# Revit family: Grease_Interceptor-MIFAB-BIG-500 (1)
name_source: partatom
category: Specialty Equipment
units: mm (PartAtom-declared; Revit-internal decimal feet)

## family parameters
Always vertical = No
Cut with Voids When Loaded = No
OmniClass Number = 23.70.50.14.21.14
OmniClass Title = Grease Interceptor
Part Type = Normal
Room Calculation Point = No
Round Connector Dimension = Use Diameter
Shared = Yes
Work Plane-Based = Yes

## types (1)
- BIG-500
    Assembly Code = D2030400
    Default Elevation = 0"
    Description = MIFAB® Series BIG 500 HDPE rotational molded grease interceptor with flow rating of 50 GPM and liquid holding capacity of 55
gallons.
    Finish (Body) = Plastic-MIFAB-Polyethylene
    Finish (Lid) = Metal-MIFAB-Steel
    Finish (Pipe) = Metal-MIFAB-Stainless Steel
    Flow Rate = 50 GPM
    Grease Design Capacity = 250 Lbs. (35 Gallons)
    IAPMO Compliance = Compliance with International Plumbing Code (I.P.C.) / I.C.C.
    Installation Type = On or In Floor
    Length = 37"
    Liquid Holding Capacity = 55 Gallons (7.19 Cu. Ft.)
    Manufacturer = MIFAB
    Model = BIG-500
    Price = Prices may vary. Please consult Manufacturer Representative for most up-to-date price list.
    Product Documentation Link = https://www.mifab.com
    Product Page URL = https://www.mifab.com
    Sediment Capacity = 28 Gallons
    Shipping Weight = 90 lb
    URL = https://www.mifab.com
    Waste Connection Diameter = 4"
    Waste Connection Radius = 2"
    Width = 28"

## geometry (parser evidence)
native form markers: Sweep x2
no freeform markers — native parametric forms only
